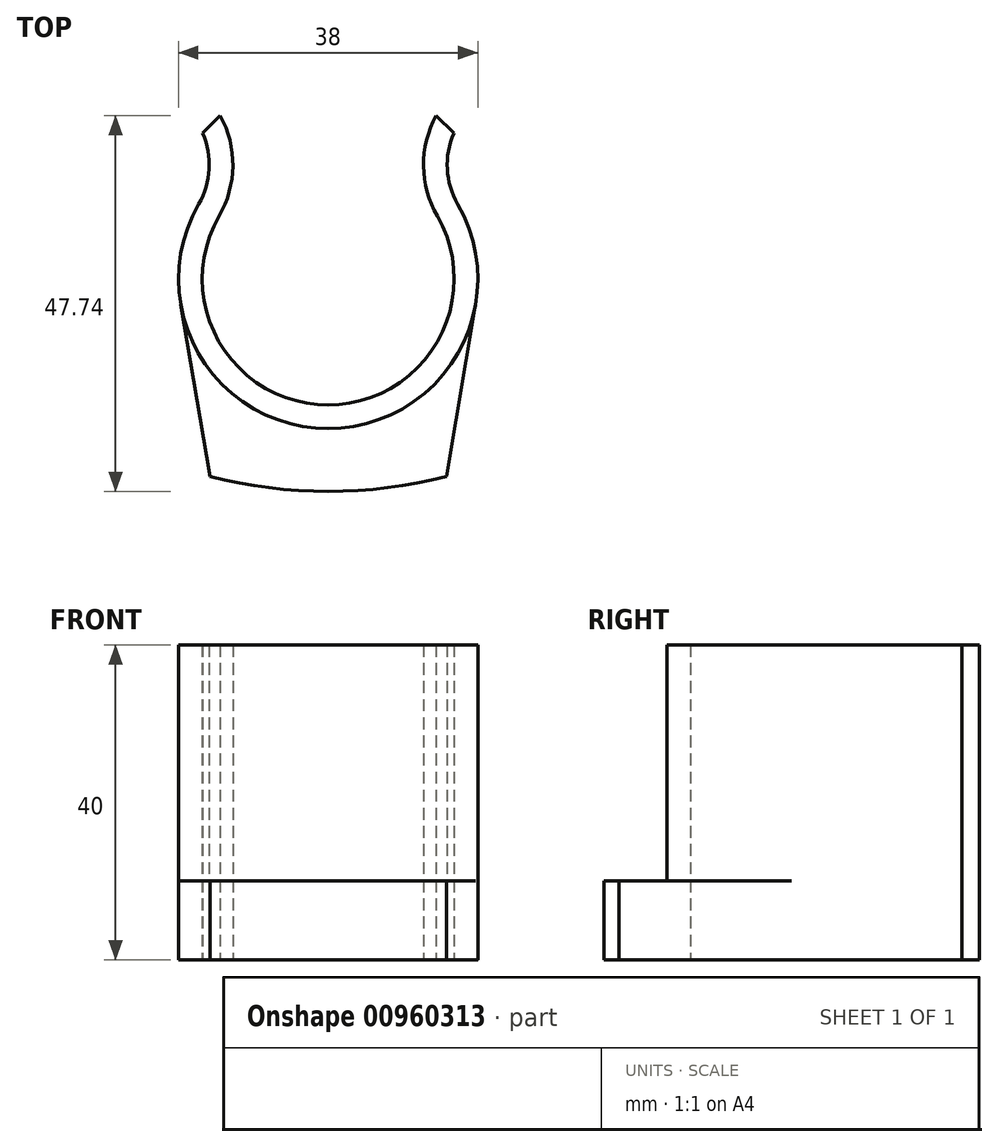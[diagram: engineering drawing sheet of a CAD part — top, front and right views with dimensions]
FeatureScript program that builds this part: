
annotation { "Feature Type Name" : "Feature", "Feature Type Description" : "" }
export const myFeature = defineFeature(function(context is Context, id is Id, definition is map)
    precondition{}
    {
        {
            var Q0;
            Q0=qCreatedBy(makeId("Top.planeOp"),FACE);
            var sketch = newSketch(context, id + "F0", { "sketchPlane" : qUnion([Q0])});
            skArc(sketch, "E0", {"start": v(-13.86, 8) * mm, "mid": v(0, -16) * mm, "end": v(13.86, 8) * mm});
            skLineSegment(sketch, "E1", {"start": v(-13.86, 8) * mm, "end": v(13.86, 8) * mm, "construction": true});
            skLineSegment(sketch, "E2", {"start": v(0, 0) * mm, "end": v(13.86, 8) * mm, "construction": true});
            skLineSegment(sketch, "E3", {"start": v(0, 0) * mm, "end": v(-13.86, 8) * mm, "construction": true});
            skLineSegment(sketch, "E4", {"start": v(13.86, 8) * mm, "end": v(15.55, 10.92) * mm});
            skLineSegment(sketch, "E5", {"start": v(-13.86, 8) * mm, "end": v(-15.55, 10.92) * mm});
            skArc(sketch, "E6", {"start": v(-15.55, 10.92) * mm, "mid": v(0, -19) * mm, "end": v(15.55, 10.92) * mm});
            skSolve(sketch);
        }
        {
            var Q0;
            Q0 = qSketchRegion(id + "F0", true);
            extrude(context, id + "F1", {"entities" : qUnion([Q0]), "depth" : 40 * mm, "offsetDistance" : 25 * mm});
        }
        {
            var Q0;
            Q0=qCreatedBy(makeId("Top.planeOp"),FACE);
            var sketch = newSketch(context, id + "F2", { "sketchPlane" : qUnion([Q0])});
            skArc(sketch, "E7", {"start": v(13.71, 20.74) * mm, "mid": v(12.12, 14.35) * mm, "end": v(13.86, 8) * mm});
            skArc(sketch, "E8", {"start": v(15.95, 18.5) * mm, "mid": v(15.13, 13.94) * mm, "end": v(16.45, 9.5) * mm});
            skLineSegment(sketch, "E9", {"start": v(15.95, 18.5) * mm, "end": v(13.71, 20.74) * mm});
            skLineSegment(sketch, "E10", {"start": v(13.86, 8) * mm, "end": v(16.45, 9.5) * mm});
            skLineSegment(sketch, "E11", {"start": v(0, 0) * mm, "end": v(0, 14.97) * mm, "construction": true});
            skSolve(sketch);
        }
        {
            var Q0;
            Q0=makeQuery(id+"F2.imprint","IMPRINT",FACE,{"disambiguationData":[TD([[makeQuery(id+"F2.imprint","IMPRINT",EDGE,{"derivedFrom":sQuery(id+"F2.wireOp",EDGE,"E7")}),1.0]])]});
            var Q1;
            Q1=makeQuery(id+"F1.opExtrude","CAP_FACE",FACE,{"disambiguationData":[OSD([sQuery(id+"F0.wireOp",EDGE,"E0"),sQuery(id+"F0.wireOp",EDGE,"E4"),sQuery(id+"F0.wireOp",EDGE,"E5"),sQuery(id+"F0.wireOp",EDGE,"E6")])],"isStart":false});
            extrude(context, id + "F3", {"entities" : qUnion([Q0]), "operationType" : NewBodyOperationType.ADD, "endBound" : BoundingType.UP_TO_SURFACE, "depth" : 25 * mm, "endBoundEntityFace" : qUnion([Q1]), "offsetDistance" : 25 * mm});
        }
        {
            var Q0;
            Q0=makeQuery(id+"F1.opExtrude","SWEPT_BODY",BODY,{"disambiguationData":[OSD([sQuery(id+"F0.wireOp",EDGE,"E0"),sQuery(id+"F0.wireOp",EDGE,"E4"),sQuery(id+"F0.wireOp",EDGE,"E5"),sQuery(id+"F0.wireOp",EDGE,"E6")])]});
            var Q1;
            Q1=qCreatedBy(makeId("Right.planeOp"),FACE);
            mirror(context, id + "F4", {"operationType" : NewBodyOperationType.ADD, "entities" : qUnion([Q0]), "mirrorPlane" : qUnion([Q1])});
        }
        {
            var Q0;
            {var subQ0=makeQuery(id+"F3.boolean.opBoolean","MERGE",FACE,{"derivedFrom":[makeQuery(id+"F1.opExtrude","CAP_FACE",FACE,{"disambiguationData":[OSD([sQuery(id+"F0.wireOp",EDGE,"E0"),sQuery(id+"F0.wireOp",EDGE,"E4"),sQuery(id+"F0.wireOp",EDGE,"E5"),sQuery(id+"F0.wireOp",EDGE,"E6")])],"isStart":true}),makeQuery(id+"F3.opExtrude","CAP_FACE",FACE,{"disambiguationData":[OSD([sQuery(id+"F2.wireOp",EDGE,"E7"),sQuery(id+"F2.wireOp",EDGE,"E8"),sQuery(id+"F2.wireOp",EDGE,"E9"),sQuery(id+"F2.wireOp",EDGE,"E10")])],"isStart":true})]});Q0=makeQuery(id+"F4.boolean.opBoolean","MERGE",FACE,{"derivedFrom":[subQ0,makeQuery(id+"F4.opPattern","COPY",FACE,{"derivedFrom":subQ0,"instanceName":"1"})]});}
            var sketch = newSketch(context, id + "F5", { "sketchPlane" : qUnion([Q0])});
            skArc(sketch, "E12", {"start": v(18.73, 3.19) * mm, "mid": v(0, 19) * mm, "end": v(-18.73, 3.19) * mm});
            skArc(sketch, "E13", {"start": v(15, 25.1) * mm, "mid": v(0, 27) * mm, "end": v(-15, 25.1) * mm});
            skLineSegment(sketch, "E14", {"start": v(18.73, 3.19) * mm, "end": v(15, 25.1) * mm});
            skLineSegment(sketch, "E15", {"start": v(-18.73, 3.19) * mm, "end": v(-15, 25.1) * mm});
            skLineSegment(sketch, "E16", {"start": v(0, 0) * mm, "end": v(0, 19) * mm, "construction": true});
            skLineSegment(sketch, "E17", {"start": v(0, 19) * mm, "end": v(0, 27) * mm, "construction": true});
            skSolve(sketch);
        }
        {
            var Q0;
            Q0 = qSketchRegion(id + "F5", true);
            extrude(context, id + "F6", {"entities" : qUnion([Q0]), "operationType" : NewBodyOperationType.ADD, "oppositeDirection" : true, "depth" : 10 * mm, "offsetDistance" : 25 * mm});
        }
    });
